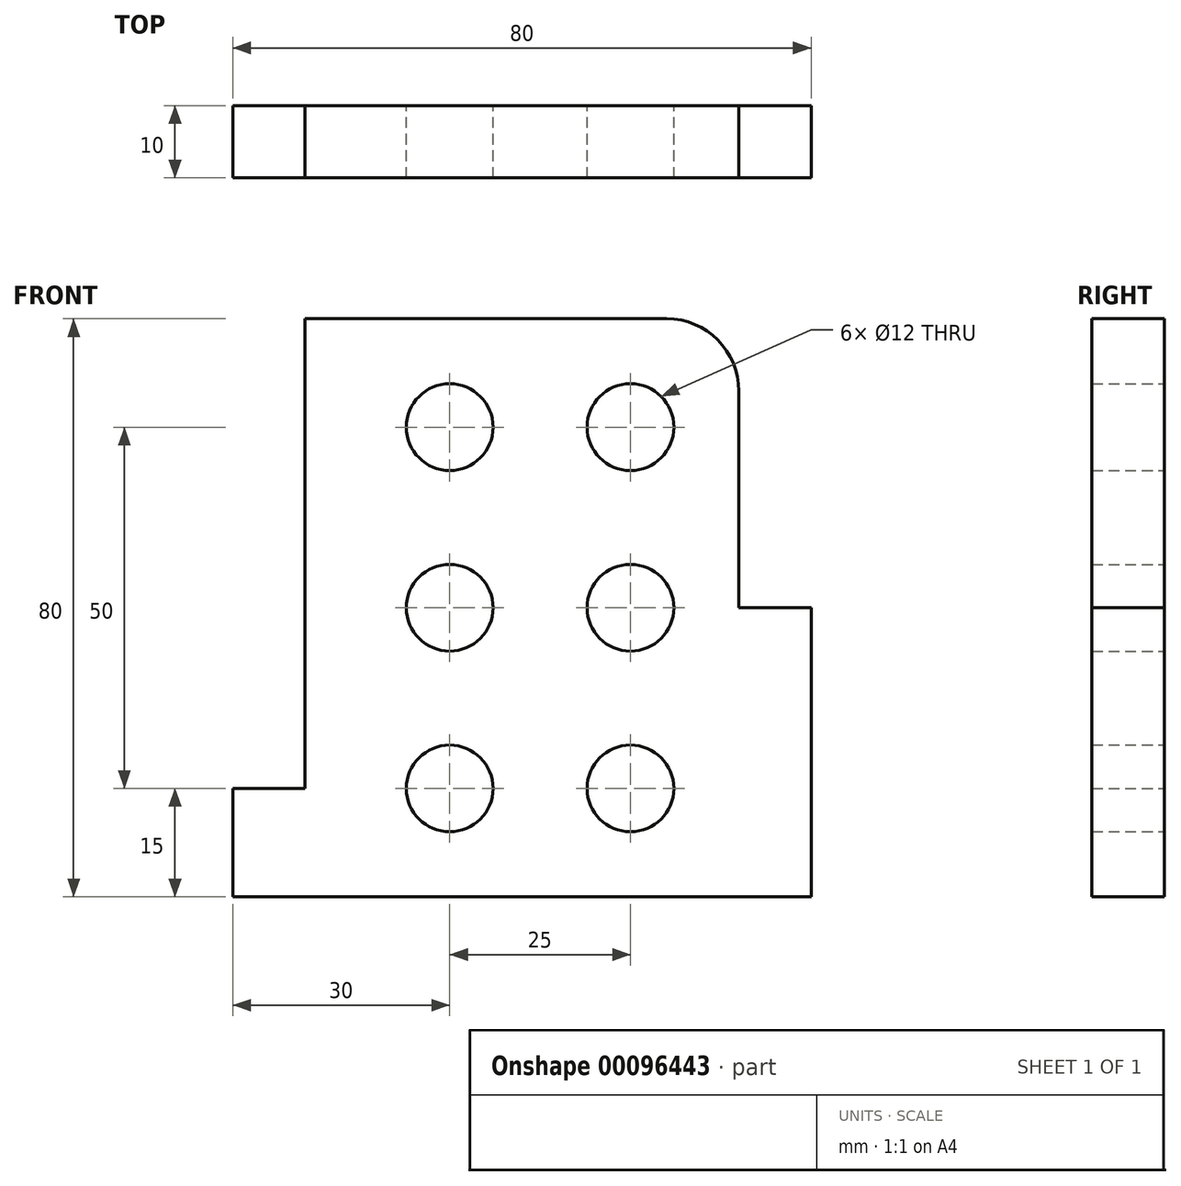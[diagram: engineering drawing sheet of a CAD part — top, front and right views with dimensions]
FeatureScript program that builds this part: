
annotation { "Feature Type Name" : "Feature", "Feature Type Description" : "" }
export const myFeature = defineFeature(function(context is Context, id is Id, definition is map)
    precondition{}
    {
        {
            var Q0;
            Q0=qCreatedBy(makeId("Front.planeOp"),FACE);
            var sketch = newSketch(context, id + "F0", { "sketchPlane" : qUnion([Q0])});
            skLineSegment(sketch, "E0", {"start": v(0, 0) * mm, "end": v(80, 0) * mm});
            skLineSegment(sketch, "E1", {"start": v(80, 0) * mm, "end": v(80, 40) * mm});
            skLineSegment(sketch, "E2", {"start": v(80, 40) * mm, "end": v(70, 40) * mm});
            skLineSegment(sketch, "E3", {"start": v(70, 40) * mm, "end": v(70, 70) * mm});
            skLineSegment(sketch, "E4", {"start": v(60, 80) * mm, "end": v(10, 80) * mm});
            skLineSegment(sketch, "E5", {"start": v(10, 80) * mm, "end": v(10, 15) * mm});
            skLineSegment(sketch, "E6", {"start": v(10, 15) * mm, "end": v(0, 15) * mm});
            skLineSegment(sketch, "E7", {"start": v(0, 15) * mm, "end": v(0, 0) * mm});
            skLineSegment(sketch, "E8", {"start": v(30, 0) * mm, "end": v(30, 80) * mm, "construction": true});
            skLineSegment(sketch, "E9", {"start": v(55, 0) * mm, "end": v(55, 80) * mm, "construction": true});
            skLineSegment(sketch, "E10", {"start": v(10, 65) * mm, "end": v(70, 65) * mm, "construction": true});
            skLineSegment(sketch, "E11", {"start": v(70, 40) * mm, "end": v(10, 40) * mm, "construction": true});
            skPoint(sketch, "E11.endSnap0", {"position": v(30, 40) * mm});
            skLineSegment(sketch, "E12", {"start": v(10, 15) * mm, "end": v(80, 15) * mm, "construction": true});
            skCircle(sketch, "E13", {"center": v(30, 65) * mm, "radius": 6 * mm});
            skCircle(sketch, "E14", {"center": v(55, 65) * mm, "radius": 6 * mm});
            skCircle(sketch, "E15", {"center": v(55, 40) * mm, "radius": 6 * mm});
            skCircle(sketch, "E16", {"center": v(30, 40) * mm, "radius": 6 * mm});
            skCircle(sketch, "E17", {"center": v(30, 15) * mm, "radius": 6 * mm});
            skCircle(sketch, "E18", {"center": v(55, 15) * mm, "radius": 6 * mm});
            skPoint(sketch, "E19.visualSharp", {"position": v(70, 80) * mm});
            skArc(sketch, "E19.filletArc", {"start": v(70, 70) * mm, "mid": v(67.07, 77.07) * mm, "end": v(60, 80) * mm});
            skSolve(sketch);
        }
        {
            var Q0;
            Q0 = qSketchRegion(id + "F0", true);
            extrude(context, id + "F1", {"entities" : qUnion([Q0]), "depth" : 10 * mm});
        }
    });
